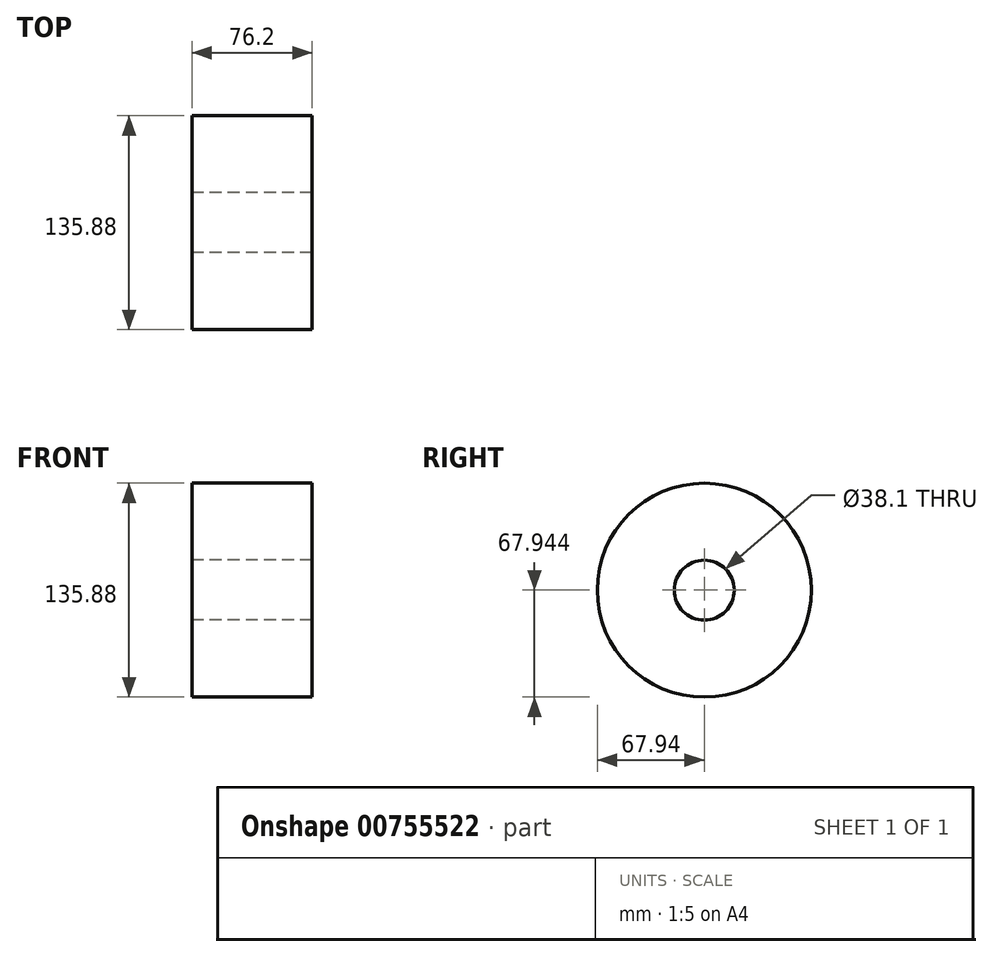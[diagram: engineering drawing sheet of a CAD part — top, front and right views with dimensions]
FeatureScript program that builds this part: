
annotation { "Feature Type Name" : "Feature", "Feature Type Description" : "" }
export const myFeature = defineFeature(function(context is Context, id is Id, definition is map)
    precondition{}
    {
        {
            var Q0;
            Q0=qCreatedBy(makeId("Right.planeOp"),FACE);
            var sketch = newSketch(context, id + "F0", { "sketchPlane" : qUnion([Q0])});
            skCircle(sketch, "E0", {"center": v(0, -9.02) * mm, "radius": 19.05 * mm});
            skCircle(sketch, "E1", {"center": v(0, -9.02) * mm, "radius": 67.94 * mm});
            skSolve(sketch);
        }
        {
            var Q0;
            Q0 = qSketchRegion(id + "F0", true);
            extrude(context, id + "F1", {"entities" : qUnion([Q0]), "depth" : 76.2 * mm, "offsetDistance" : 25.4 * mm});
        }
    });
